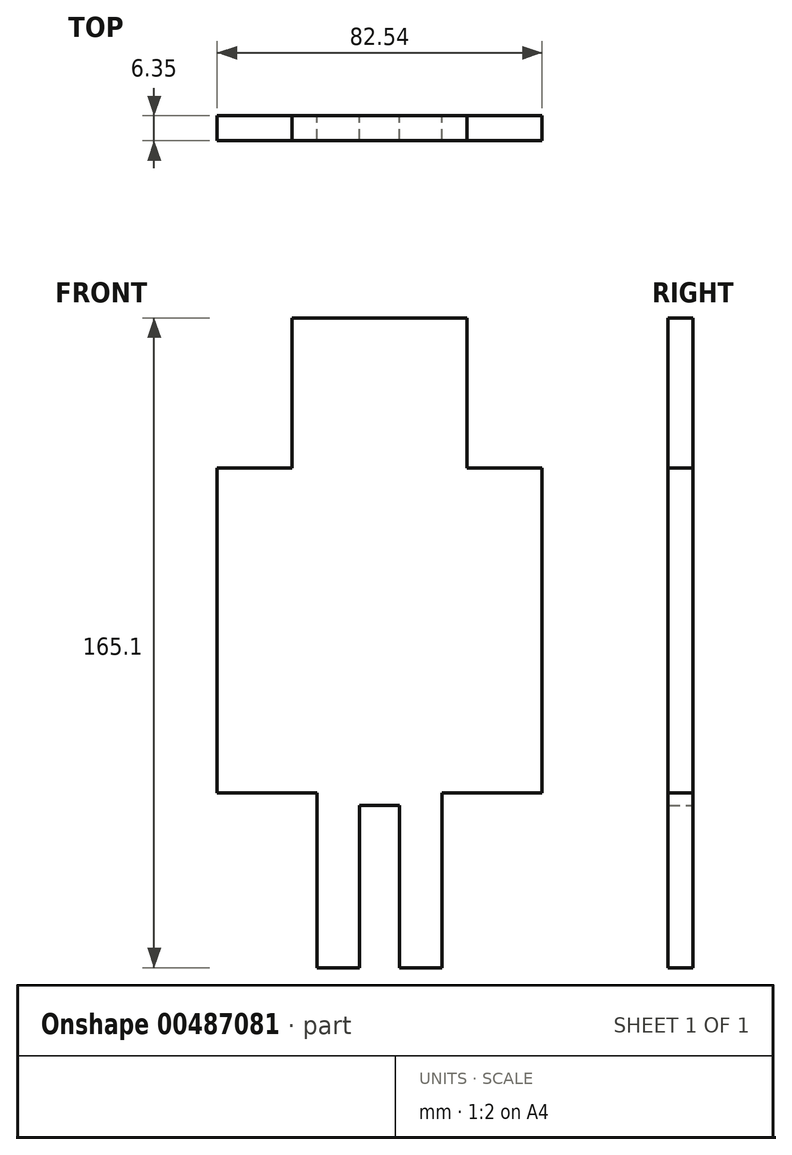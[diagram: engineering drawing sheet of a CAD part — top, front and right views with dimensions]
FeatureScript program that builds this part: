
annotation { "Feature Type Name" : "Feature", "Feature Type Description" : "" }
export const myFeature = defineFeature(function(context is Context, id is Id, definition is map)
    precondition{}
    {
        {
            var Q0;
            Q0=qCreatedBy(makeId("Front.planeOp"),FACE);
            var sketch = newSketch(context, id + "F0", { "sketchPlane" : qUnion([Q0])});
            skLineSegment(sketch, "E0.bottom", {"start": v(15.88, -82.55) * mm, "end": v(5.08, -82.55) * mm});
            skLineSegment(sketch, "E0.top", {"start": v(22.23, 82.55) * mm, "end": v(-22.23, 82.55) * mm});
            skLineSegment(sketch, "E0.left", {"start": v(41.28, -38.1) * mm, "end": v(41.28, 44.45) * mm});
            skLineSegment(sketch, "E0.right", {"start": v(-41.28, -38.1) * mm, "end": v(-41.27, 44.45) * mm});
            skPoint(sketch, "E0.middle", {"position": v(0, 0) * mm});
            skLineSegment(sketch, "E1.bottom", {"start": v(-22.23, 82.55) * mm, "end": v(22.23, 82.55) * mm});
            skLineSegment(sketch, "E2.top", {"start": v(-41.27, 44.45) * mm, "end": v(-22.22, 44.45) * mm});
            skLineSegment(sketch, "E2.right", {"start": v(-22.23, 82.55) * mm, "end": v(-22.22, 44.45) * mm});
            skLineSegment(sketch, "E3.top", {"start": v(22.23, 44.45) * mm, "end": v(41.28, 44.45) * mm});
            skLineSegment(sketch, "E3.left", {"start": v(22.23, 82.55) * mm, "end": v(22.23, 44.45) * mm});
            skPoint(sketch, "E4.orphan", {"position": v(-41.27, 44.45) * mm});
            skPoint(sketch, "E5.orphan", {"position": v(41.28, 82.55) * mm});
            skLineSegment(sketch, "E6", {"start": v(-41.28, -38.1) * mm, "end": v(-15.87, -38.1) * mm});
            skLineSegment(sketch, "E7.right", {"start": v(-15.87, -82.55) * mm, "end": v(-15.87, -38.1) * mm});
            skLineSegment(sketch, "E8.top", {"start": v(41.28, -38.1) * mm, "end": v(15.88, -38.1) * mm});
            skLineSegment(sketch, "E8.right", {"start": v(15.88, -82.55) * mm, "end": v(15.88, -38.1) * mm});
            skPoint(sketch, "E9.orphan", {"position": v(-41.28, -82.55) * mm});
            skLineSegment(sketch, "E10.top", {"start": v(-5.08, -41.28) * mm, "end": v(5.08, -41.28) * mm});
            skLineSegment(sketch, "E10.left", {"start": v(-5.08, -82.55) * mm, "end": v(-5.08, -41.28) * mm});
            skLineSegment(sketch, "E10.right", {"start": v(5.08, -82.55) * mm, "end": v(5.08, -41.28) * mm});
            skLineSegment(sketch, "E11.trimOffspring", {"start": v(15.88, -38.1) * mm, "end": v(41.28, -38.1) * mm});
            skLineSegment(sketch, "E12.trimOffspring", {"start": v(-5.08, -82.55) * mm, "end": v(-15.87, -82.55) * mm});
            skSolve(sketch);
        }
        {
            var Q0;
            Q0 = qSketchRegion(id + "F0", true);
            extrude(context, id + "F1", {"entities" : qUnion([Q0]), "depth" : 6.35 * mm});
        }
    });
